# Revit family: Furniture-Counter_Top-KOHLER-Solid_Expressions-K-5421_1
name_source: partatom
category: Specialty Equipment
units: mm (PartAtom-declared; Revit-internal decimal feet)

## family parameters
Cut with Voids When Loaded = No
Host = Face
OmniClass Number = 23.31.25.00
OmniClass Title = Toilet and Bath Specialties
Part Type = Normal
Room Calculation Point = No
Round Connector Dimension = Use Diameter
Shared = No

## types (4) — shared parameters
ADA Compliant = No
Assembly Code = C1030200
Date Modified = 08/23/2023
Default Elevation = 42"
Description = 25 Inch Vanity Top With Single Verticyl Oval Cutout
Height = 1 1/4"
Length = 22 13/16"
Manufacturer = Kohler Co.
Master Format 2014 = 10 28 00
Master Format 2014 Name = Toilet, Bath, and Laundry Accessories
Material = Solid Surface
Product Documentation Link = https://www.us.kohler.com
Product Name = Solid Expressions
Product Page URL = http://www.us.kohler.com
URL = https://www.us.kohler.com
WaterSense Certified = No
Width = 25 5/8"

## per-type parameters (varying)
| type | Finish | Model | Type |
| S34-Almond Expressions | Kohler-Solid_Surface-S34-Almond_Expressions | K-5421-S34 | 2 |
| S35-Biscuit Expressions | Kohler-Solid_Surface-S35-Biscuit_Expressions | K-5421-S35 | 3 |
| S36-Ice Grey Expressions | Kohler-Solid_Surface-S36-Ice_Grey_Expressions | K-5421-S36 | 4 |
| S33-White Expressions | Kohler-Solid_Surface-S33-White_Expressions | K-5421-S33 | 1 |

## geometry (parser evidence)
native form markers: Sweep x4
no freeform markers — native parametric forms only
